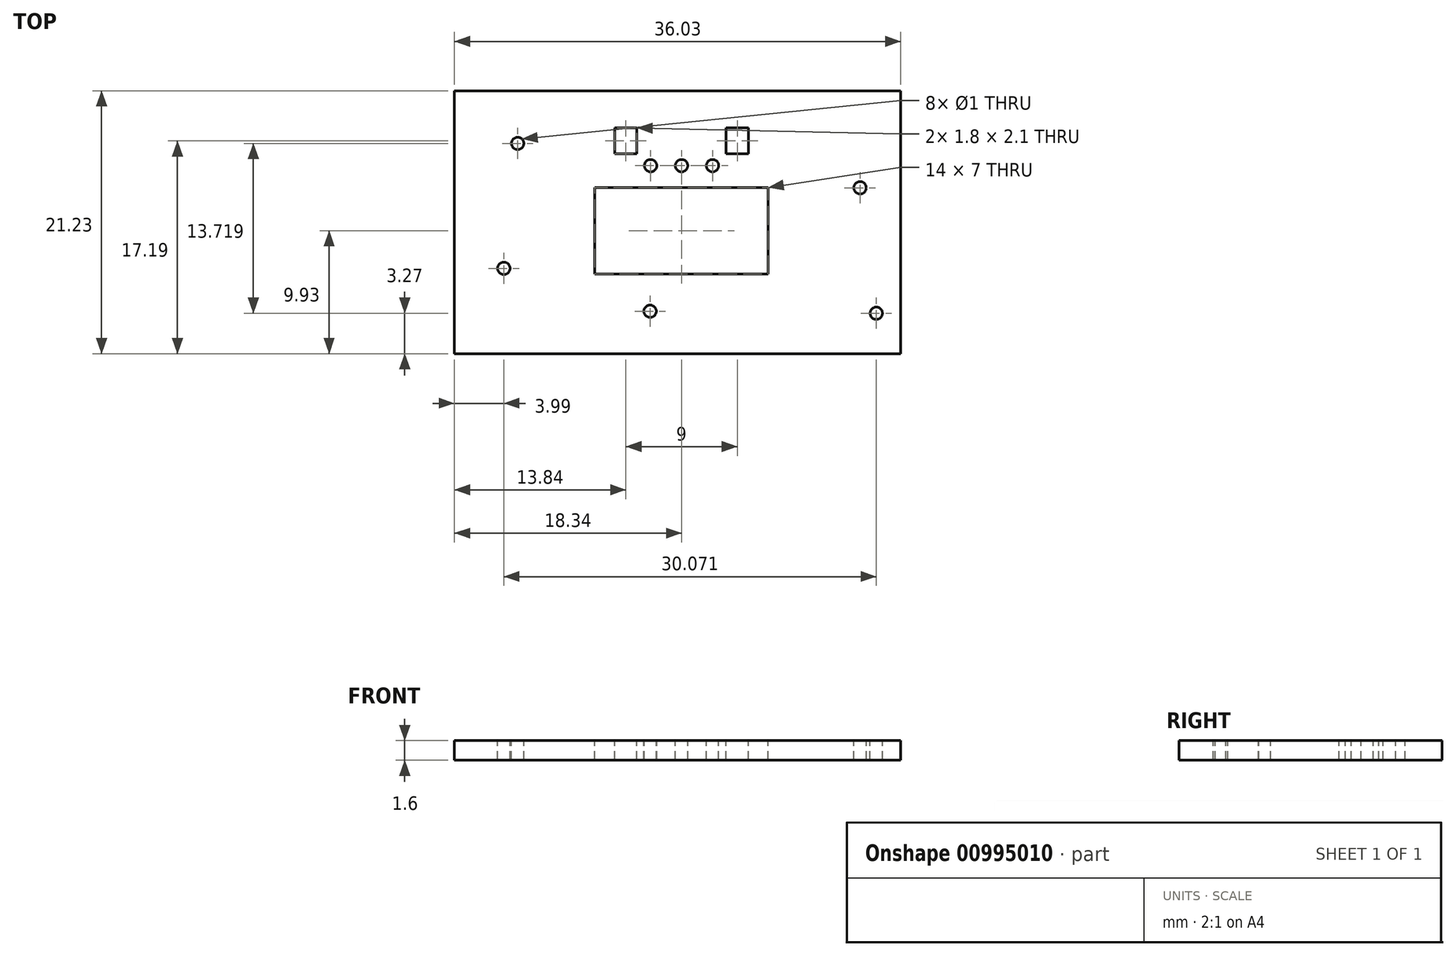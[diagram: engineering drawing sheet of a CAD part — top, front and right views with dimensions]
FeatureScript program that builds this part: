
annotation { "Feature Type Name" : "Feature", "Feature Type Description" : "" }
export const myFeature = defineFeature(function(context is Context, id is Id, definition is map)
    precondition{}
    {
        {
            var Q0;
            Q0=qCreatedBy(makeId("Top.planeOp"),FACE);
            var sketch = newSketch(context, id + "F0", { "sketchPlane" : qUnion([Q0])});
            skLineSegment(sketch, "E0.bottom", {"start": v(-18.34, 11.3) * mm, "end": v(17.69, 11.3) * mm});
            skLineSegment(sketch, "E0.top", {"start": v(-18.34, -9.93) * mm, "end": v(17.69, -9.93) * mm});
            skLineSegment(sketch, "E0.left", {"start": v(-18.34, 11.3) * mm, "end": v(-18.34, -9.93) * mm});
            skLineSegment(sketch, "E0.right", {"start": v(17.69, 11.3) * mm, "end": v(17.69, -9.93) * mm});
            skCircle(sketch, "E1", {"center": v(0, 5.26) * mm, "radius": 0.5 * mm});
            skCircle(sketch, "E2", {"center": v(-2.5, 5.26) * mm, "radius": 0.5 * mm});
            skCircle(sketch, "E3", {"center": v(2.5, 5.26) * mm, "radius": 0.5 * mm});
            skCircle(sketch, "E4", {"center": v(-2.54, -6.5) * mm, "radius": 0.5 * mm});
            skLineSegment(sketch, "E5.bottom", {"start": v(-5.4, 8.3) * mm, "end": v(-3.6, 8.3) * mm});
            skLineSegment(sketch, "E5.top", {"start": v(-5.4, 6.2) * mm, "end": v(-3.6, 6.2) * mm});
            skLineSegment(sketch, "E5.left", {"start": v(-5.4, 8.3) * mm, "end": v(-5.4, 6.2) * mm});
            skLineSegment(sketch, "E5.right", {"start": v(-3.6, 8.3) * mm, "end": v(-3.6, 6.2) * mm});
            skLineSegment(sketch, "E6", {"start": v(0, 0.55) * mm, "end": v(0, 1.75) * mm});
            skLineSegment(sketch, "E7.MirrorCS", {"start": v(5.4, 6.2) * mm, "end": v(3.6, 6.2) * mm});
            skLineSegment(sketch, "E8.MirrorCS", {"start": v(5.4, 8.31) * mm, "end": v(5.4, 6.2) * mm});
            skLineSegment(sketch, "E9.MirrorCS", {"start": v(3.6, 8.31) * mm, "end": v(3.6, 6.2) * mm});
            skLineSegment(sketch, "E10.MirrorCS", {"start": v(5.4, 8.3) * mm, "end": v(3.6, 8.3) * mm});
            skPoint(sketch, "E11", {"position": v(-3.6, 7.26) * mm});
            skCircle(sketch, "E12", {"center": v(-13.23, 7.06) * mm, "radius": 0.5 * mm});
            skCircle(sketch, "E13", {"center": v(14.41, 3.47) * mm, "radius": 0.5 * mm});
            skCircle(sketch, "E14", {"center": v(15.72, -6.66) * mm, "radius": 0.5 * mm});
            skCircle(sketch, "E15", {"center": v(-14.35, -3.03) * mm, "radius": 0.5 * mm});
            skSolve(sketch);
        }
        {
            var Q0;
            Q0=qSketchRegion(id+"F0",true);
            extrude(context, id + "F1", {"entities" : qUnion([Q0]), "oppositeDirection" : true, "depth" : 1.6 * mm, "offsetDistance" : 25 * mm});
        }
        {
            var Q0;
            Q0=makeQuery(id+"F1.opExtrude","CAP_FACE",FACE,{"disambiguationData":[OSD([sQuery(id+"F0.wireOp",EDGE,"E0.bottom"),sQuery(id+"F0.wireOp",EDGE,"E0.top"),sQuery(id+"F0.wireOp",EDGE,"E0.left"),sQuery(id+"F0.wireOp",EDGE,"E0.right"),sQuery(id+"F0.wireOp",EDGE,"E1"),sQuery(id+"F0.wireOp",EDGE,"E2"),sQuery(id+"F0.wireOp",EDGE,"E3"),sQuery(id+"F0.wireOp",EDGE,"E4"),sQuery(id+"F0.wireOp",EDGE,"E5.bottom"),sQuery(id+"F0.wireOp",EDGE,"E5.top"),sQuery(id+"F0.wireOp",EDGE,"E5.left"),sQuery(id+"F0.wireOp",EDGE,"E5.right"),sQuery(id+"F0.wireOp",EDGE,"E7.MirrorCS"),sQuery(id+"F0.wireOp",EDGE,"E8.MirrorCS"),sQuery(id+"F0.wireOp",EDGE,"E9.MirrorCS"),sQuery(id+"F0.wireOp",EDGE,"E10.MirrorCS")])],"isStart":true});
            var sketch = newSketch(context, id + "F2", { "sketchPlane" : qUnion([Q0])});
            skLineSegment(sketch, "E16.bottom", {"start": v(7, 3.5) * mm, "end": v(-7, 3.5) * mm});
            skLineSegment(sketch, "E16.top", {"start": v(7, -3.5) * mm, "end": v(-7, -3.5) * mm});
            skLineSegment(sketch, "E16.left", {"start": v(7, 3.5) * mm, "end": v(7, -3.5) * mm});
            skLineSegment(sketch, "E16.right", {"start": v(-7, 3.5) * mm, "end": v(-7, -3.5) * mm});
            skPoint(sketch, "E16.middle", {"position": v(0, 0) * mm});
            skSolve(sketch);
        }
        {
            var Q0;
            Q0=qSketchRegion(id+"F2",true);
            extrude(context, id + "F3", {"entities" : qUnion([Q0]), "operationType" : NewBodyOperationType.REMOVE, "oppositeDirection" : true, "depth" : 25 * mm, "offsetDistance" : 25 * mm});
        }
    });
